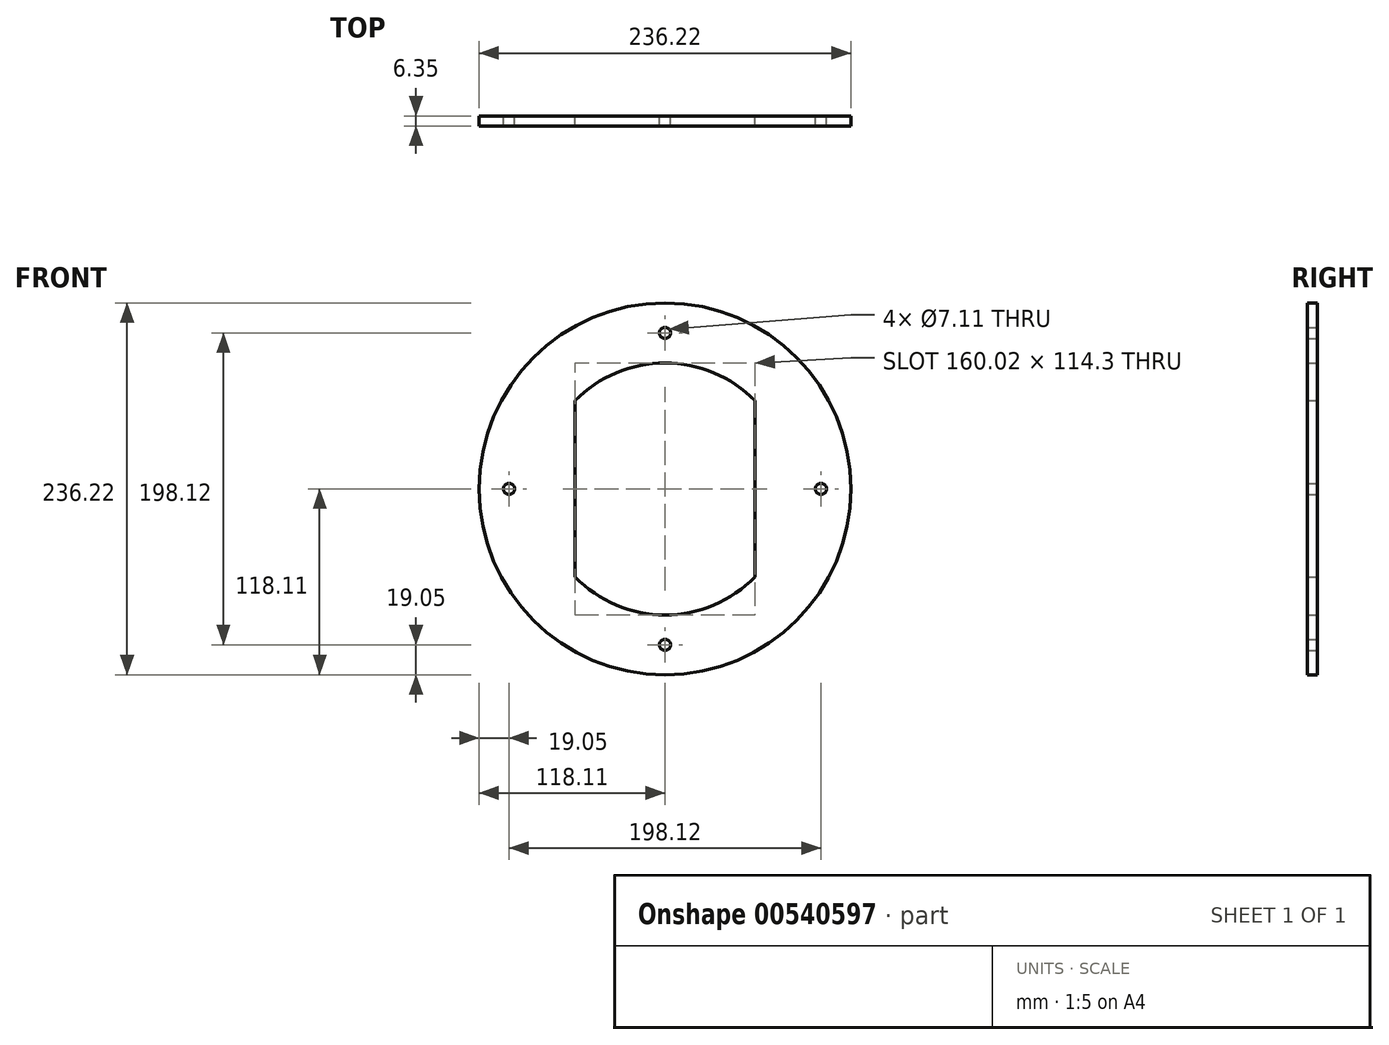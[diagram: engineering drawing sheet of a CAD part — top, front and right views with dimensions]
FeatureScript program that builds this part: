
annotation { "Feature Type Name" : "Feature", "Feature Type Description" : "" }
export const myFeature = defineFeature(function(context is Context, id is Id, definition is map)
    precondition{}
    {
        {
            var Q0;
            Q0=qCreatedBy(makeId("Front.planeOp"),FACE);
            var sketch = newSketch(context, id + "F0", { "sketchPlane" : qUnion([Q0])});
            skArc(sketch, "E0", {"start": v(-57.15, -56) * mm, "mid": v(0, -80) * mm, "end": v(57.15, -56) * mm});
            skCircle(sketch, "E1", {"center": v(0, 0) * mm, "radius": 118.11 * mm});
            skCircle(sketch, "E2", {"center": v(0, 0) * mm, "radius": 99.06 * mm, "construction": true});
            skCircle(sketch, "E3", {"center": v(0, 99.06) * mm, "radius": 3.56 * mm});
            skCircle(sketch, "E4.1.0", {"center": v(-99.06, 0) * mm, "radius": 3.56 * mm});
            skCircle(sketch, "E4.2.0", {"center": v(0, -99.06) * mm, "radius": 3.56 * mm});
            skCircle(sketch, "E4.3.0", {"center": v(99.06, 0) * mm, "radius": 3.56 * mm});
            skLineSegment(sketch, "E5", {"start": v(-57.15, 56) * mm, "end": v(-57.15, -56) * mm});
            skLineSegment(sketch, "E6.MirrorCS", {"start": v(57.15, 56) * mm, "end": v(57.15, -56) * mm});
            skArc(sketch, "E7.trimOffspring", {"start": v(57.15, 56) * mm, "mid": v(0, 80) * mm, "end": v(-57.15, 56) * mm});
            skSolve(sketch);
        }
        {
            var Q0;
            {var subQ0=sQuery(id+"F0.wireOp",EDGE,"E5");Q0=makeQuery(id+"F0.imprint","IMPRINT",FACE,{"disambiguationData":[TD([[makeQuery(id+"F0.imprint","IMPRINT",EDGE,{"derivedFrom":subQ0}),-1.0]])]});}
            var Q1;
            {var subQ0=sQuery(id+"F0.wireOp",EDGE,"E6.MirrorCS");Q1=makeQuery(id+"F0.imprint","IMPRINT",FACE,{"disambiguationData":[TD([[makeQuery(id+"F0.imprint","IMPRINT",EDGE,{"derivedFrom":subQ0}),1.0]])]});}
            var Q2;
            Q2=makeQuery(id+"F0.imprint","IMPRINT",FACE,{"disambiguationData":[TD([[makeQuery(id+"F0.imprint","IMPRINT",EDGE,{"derivedFrom":sQuery(id+"F0.wireOp",EDGE,"E1")}),1.0]])]});
            extrude(context, id + "F1", {"entities" : qUnion([Q0, Q1, Q2]), "depth" : 6.35 * mm, "offsetDistance" : 25.4 * mm});
        }
    });
